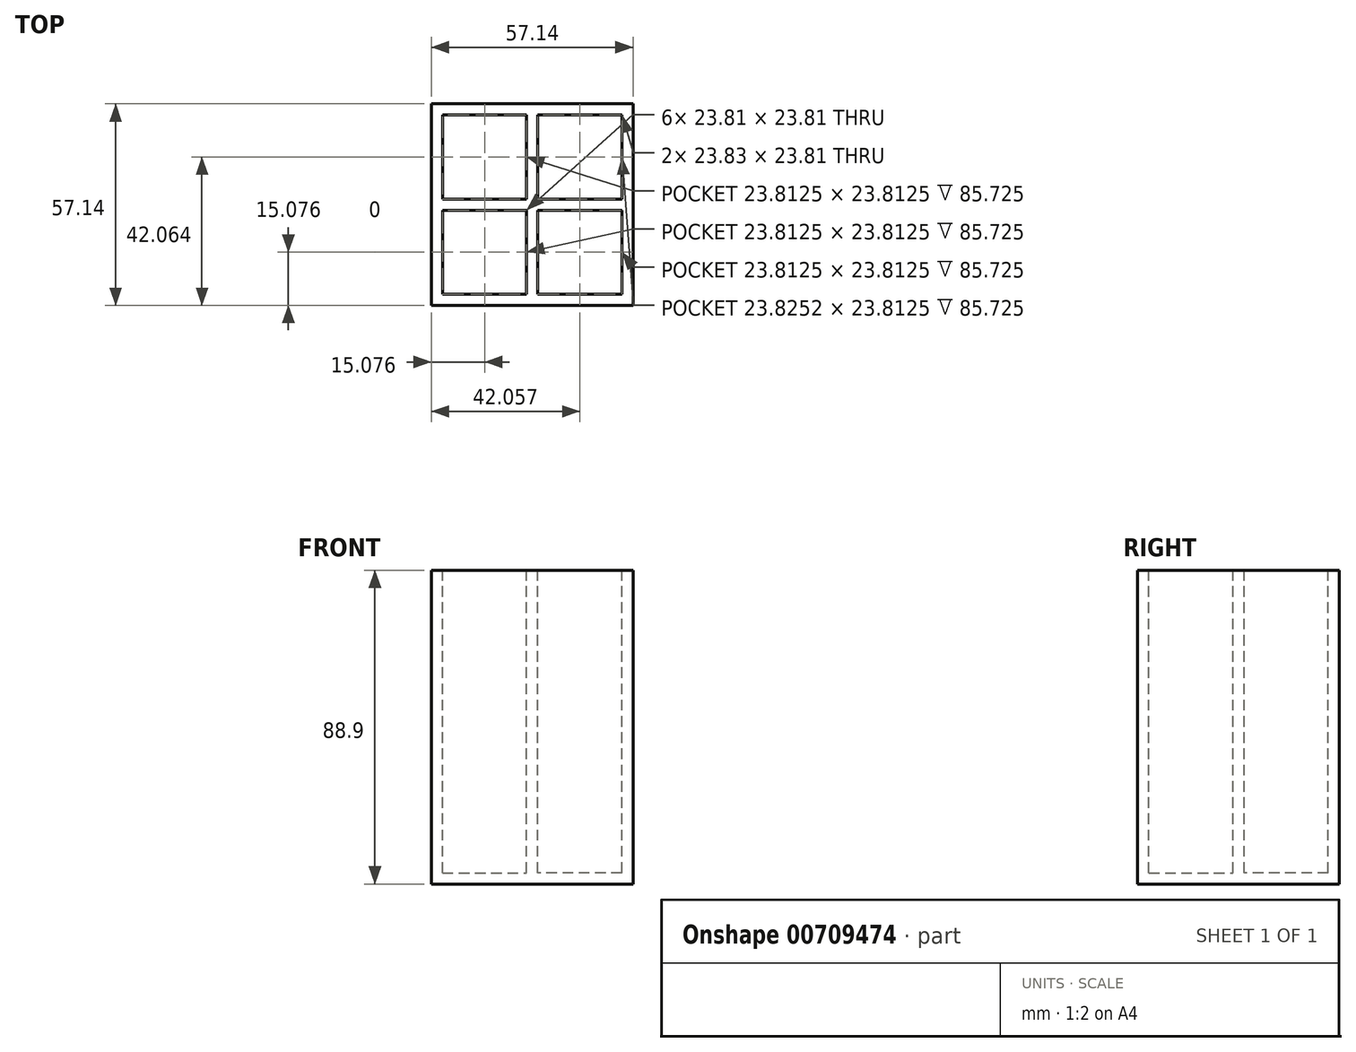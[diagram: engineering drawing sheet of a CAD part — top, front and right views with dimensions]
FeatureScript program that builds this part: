
annotation { "Feature Type Name" : "Feature", "Feature Type Description" : "" }
export const myFeature = defineFeature(function(context is Context, id is Id, definition is map)
    precondition{}
    {
        {
            var Q0;
            Q0=qCreatedBy(makeId("Top.planeOp"),FACE);
            var sketch = newSketch(context, id + "F0", { "sketchPlane" : qUnion([Q0])});
            skLineSegment(sketch, "E0.bottom", {"start": v(28.58, 28.58) * mm, "end": v(-28.57, 28.58) * mm});
            skLineSegment(sketch, "E0.top", {"start": v(28.57, -28.58) * mm, "end": v(-28.58, -28.58) * mm});
            skLineSegment(sketch, "E0.left", {"start": v(28.58, 28.58) * mm, "end": v(28.57, -28.58) * mm});
            skLineSegment(sketch, "E0.right", {"start": v(-28.57, 28.58) * mm, "end": v(-28.58, -28.58) * mm});
            skPoint(sketch, "E0.middle", {"position": v(0, 0) * mm});
            skSolve(sketch);
        }
        {
            var Q0;
            Q0=qSketchRegion(id+"F0",true);
            extrude(context, id + "F1", {"entities" : qUnion([Q0]), "depth" : 88.9 * mm, "offsetDistance" : 25.4 * mm});
        }
        {
            var Q0;
            Q0=makeQuery(id+"F1.opExtrude","CAP_FACE",FACE,{"disambiguationData":[OSD([sQuery(id+"F0.wireOp",EDGE,"E0.bottom"),sQuery(id+"F0.wireOp",EDGE,"E0.top"),sQuery(id+"F0.wireOp",EDGE,"E0.left"),sQuery(id+"F0.wireOp",EDGE,"E0.right")])],"isStart":false});
            var sketch = newSketch(context, id + "F2", { "sketchPlane" : qUnion([Q0])});
            skLineSegment(sketch, "E1.bottom", {"start": v(-25.4, 25.4) * mm, "end": v(-1.59, 25.4) * mm});
            skLineSegment(sketch, "E1.top", {"start": v(-25.4, 1.59) * mm, "end": v(-1.59, 1.59) * mm});
            skLineSegment(sketch, "E1.left", {"start": v(-25.4, 25.4) * mm, "end": v(-25.4, 1.59) * mm});
            skLineSegment(sketch, "E1.right", {"start": v(-1.59, 25.4) * mm, "end": v(-1.59, 1.59) * mm});
            skLineSegment(sketch, "E2.bottom", {"start": v(-25.4, -25.4) * mm, "end": v(-1.59, -25.4) * mm});
            skLineSegment(sketch, "E2.top", {"start": v(-25.4, -1.59) * mm, "end": v(-1.59, -1.59) * mm});
            skLineSegment(sketch, "E2.left", {"start": v(-25.4, -25.4) * mm, "end": v(-25.4, -1.59) * mm});
            skLineSegment(sketch, "E2.right", {"start": v(-1.59, -25.4) * mm, "end": v(-1.59, -1.59) * mm});
            skLineSegment(sketch, "E3.bottom", {"start": v(25.4, -25.4) * mm, "end": v(1.59, -25.4) * mm});
            skLineSegment(sketch, "E3.top", {"start": v(25.4, -1.59) * mm, "end": v(1.59, -1.59) * mm});
            skLineSegment(sketch, "E3.left", {"start": v(25.4, -25.4) * mm, "end": v(25.4, -1.59) * mm});
            skLineSegment(sketch, "E3.right", {"start": v(1.59, -25.4) * mm, "end": v(1.59, -1.59) * mm});
            skLineSegment(sketch, "E4.bottom", {"start": v(25.4, 25.4) * mm, "end": v(1.57, 25.4) * mm});
            skLineSegment(sketch, "E4.top", {"start": v(25.4, 1.59) * mm, "end": v(1.57, 1.59) * mm});
            skLineSegment(sketch, "E4.left", {"start": v(25.4, 25.4) * mm, "end": v(25.4, 1.59) * mm});
            skLineSegment(sketch, "E4.right", {"start": v(1.57, 25.4) * mm, "end": v(1.57, 1.59) * mm});
            skSolve(sketch);
        }
        {
            var Q0;
            Q0=qSketchRegion(id+"F2",true);
            extrude(context, id + "F3", {"entities" : qUnion([Q0]), "operationType" : NewBodyOperationType.REMOVE, "oppositeDirection" : true, "depth" : 85.72 * mm, "offsetDistance" : 25.4 * mm});
        }
    });
